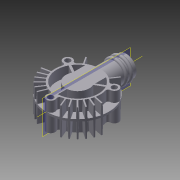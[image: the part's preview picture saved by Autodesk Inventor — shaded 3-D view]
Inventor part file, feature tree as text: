
AUTODESK INVENTOR PART (.ipt)
format: ipt  version: 2016 SP1 (Build 200210100, 210)  size: 2,439,680 bytes
history: native  units: in
note: dims shown in document units (in); Inventor stores cm internally (conversion verified against a paired STEP export)
features: sketch x24, extrude x21, pattern_circular x9, plane x4, draft x4, mirror x3, fillet x2, hole x2, revolve x2, other x1, thread x1
ambient origin geometry x8: Origin, YZ Plane, XZ Plane, XY Plane, X Axis, Y Axis, Z Axis, Center Point
bodies: Solid1 (feature_tree)
feature tree (73):
  extrude  "Extrusion1"  Depth=0.05in TaperAngle=0.0deg
  extrude  "Extrusion2"  Depth=1.08in
  extrude  "Extrusion3"  Depth=0.5in
  pattern_circular  "Circular Pattern1"  Count=3 Angle=360.0deg
  plane  "Work Plane2"
  extrude  "Extrusion17"  Depth=0.25in TaperAngle=0.0deg
  extrude  "Extrusion20"  Depth=0.25in
  draft  "FaceDraft5"
  draft  "FaceDraft6"
  fillet  "Fillet6"  Radius=0.125in
  pattern_circular  "Circular Pattern7"  Count=3 Angle=360.0deg
  extrude  "Extrusion21"  Depth=0.25in TaperAngle=360.0deg
  pattern_circular  "Circular Pattern8"  [2 undecoded]
  extrude  "Extrusion22"  Depth=0.25in
  draft  "FaceDraft7"
  draft  "FaceDraft8"
  fillet  "Fillet7"  Radius=0.125in
  pattern_circular  "Circular Pattern9"  [2 undecoded]
  extrude  "Extrusion23"  Depth=0.25in
  pattern_circular  "Circular Pattern10"  [2 undecoded]
  hole  "Hole1"  [1 undecoded]
  pattern_circular  "Circular Pattern11"  [2 undecoded]
  extrude  "Extrusion24"  Depth=0.25in
  plane  "Work Plane5"
  extrude  "Extrusion25"  Depth=0.25in TaperAngle=0.0deg
  hole  "Hole2"  [1 undecoded]
  other  "Work Axis1"
  revolve  "Revolution2"  [1 undecoded]
  pattern_circular  "Circular Pattern2"  [2 undecoded]
  extrude  "Extrusion5"  Depth=0.25in TaperAngle=360.0deg
  extrude  "Extrusion6"  Depth=0.25in
  mirror  "Mirror1"
  mirror  "Mirror2"
  extrude  "Extrusion7"  Depth=0.25in
  extrude  "Extrusion8"  Depth=0.25in TaperAngle=0.0deg
  extrude  "Extrusion9"  Depth=0.25in TaperAngle=360.0deg
  pattern_circular  "Circular Pattern3"  [2 undecoded]
  mirror  "Mirror3"
  extrude  "Extrusion10"  Depth=0.25in
  pattern_circular  "Circular Pattern4"  [2 undecoded]
  extrude  "Extrusion11"  Depth=0.25in
  plane  "Work Plane1"
  extrude  "Extrusion12"  Depth=0.25in TaperAngle=360.0deg
  extrude  "Extrusion13"  Depth=0.25in TaperAngle=0.0deg
  revolve  "Revolution1"  Angle=360.0deg
  extrude  "Extrusion14"  Depth=0.25in
  extrude  "Extrusion16"  Depth=0.25in TaperAngle=360.0deg
  thread  "Thread1"  [1 undecoded]
  sketch  "Sketch1"  dims[d0=1.5in d1=0.05in d2=0.0in]
  sketch  "Sketch2"  dims[d3=1.0in d4=1.08in]
  sketch  "Sketch3"  dims[d5=0.5625in d6=0.5in]
  sketch  "Sketch5"  dims[d7=0.25in d8=0.0in]
  sketch  "Sketch6"  dims[d9=0.05in]
  sketch  "Sketch7"  dims[d10=0.25in d11=0.0in d12=1.1811in d13=360.0deg]
  sketch  "Sketch8"  dims[d20=11.0236in d21=360.0deg d23=0.25in d24=0.0in]
  sketch  "Sketch9"  dims[d25=0.25in d26=0.0in d27=0.5in d28=0.125in d29=0.0in]
  sketch  "Sketch10"  dims[d30=1.0in]
  sketch  "Sketch11"  dims[d31=0.25in d32=0.0in]
  sketch  "Sketch12"  dims[d35=0.25in]
  sketch  "Sketch13"  dims[d36=0.2in]
  sketch  "Sketch14"  dims[d37=0.25in d38=0.0in d39=1.1811in d40=360.0deg]
  sketch  "Sketch15"  dims[d42=0.25in d43=0.0in d44=1.1811in d45=360.0deg]
  sketch  "Sketch17"  dims[d47=0.25in d48=0.0in]
  sketch  "Sketch18"  dims[d49=0.5in]
  sketch  "Sketch20"  dims[d50=0.0625in d51=0.625in d52=0.0in d53=0.0in]
  sketch  "Sketch21"  dims[d54=0.25in d55=0.0in]
  sketch  "Sketch22"  dims[d57=0.1in]
  sketch  "Sketch23"  dims[d58=0.1in]
  sketch  "Sketch24"  dims[d59=0.05in]
  plane  "Work Plane4"
  sketch  "Sketch26"  dims[d60=0.25in]
  sketch  "Sketch27"  dims[d61=0.5in]
  sketch  "Sketch28"  dims[d62=90.0deg d63=0.75in d64=0.0in d67=0.2in d68=0.125in d69=0.0in d70=1.0in d71=0.0in d72=0.25in d76=0.375in d77=0.0in d106=22.5deg d107=0.025in d108=0.025in d109=0.25in d110=0.0in d111=0.0137in d112=0.0137in d113=0.01in d114=12.5984in d115=360.0deg d117=0.1in d118=0.1in d119=0.25in d120=0.0in d121=1.1811in d122=360.0deg d124=0.25in d125=0.0in d126=0.0103in d127=0.0103in d128=0.01in d129=12.5984in d130=360.0deg d132=0.25in d133=0.0in d134=1.1811in d135=360.0deg d137=1.0in d138=1.0in d139=0.129in d140=0.75in d141=0.219in d142=0.112in d143=0.5635in d144=1.0in d145=0.8108in d146=1.1811in d147=360.0deg d149=0.125in d150=0.0in d152=-0.625in d153=0.5in d154=0.5625in d155=0.0in d156=0.313in d157=0.236in d158=0.0246in d159=0.329in d160=0.219in d161=0.112in d162=0.5635in d163=0.25in d164=0.8108in d165=0.125in d166=0.25in d167=90.0deg]
note: 18 required parameter values undecoded (feature->parameter linkage not recoverable at this tier; creation-order binding heuristic only, values carry confidence <= 0.55)